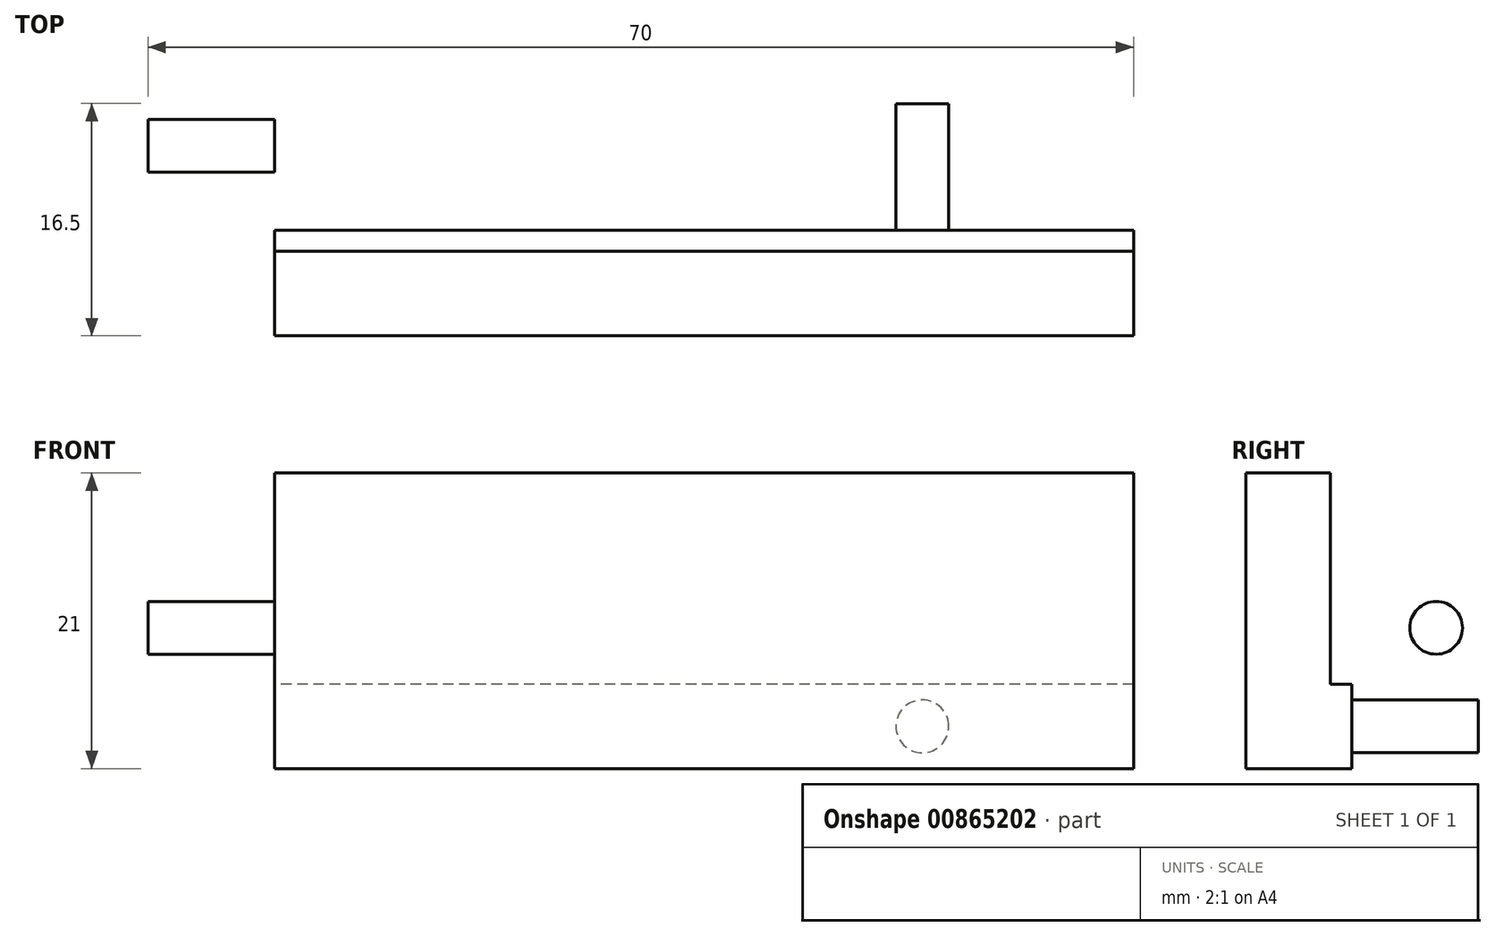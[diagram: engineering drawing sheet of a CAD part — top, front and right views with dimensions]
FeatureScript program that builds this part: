
annotation { "Feature Type Name" : "Feature", "Feature Type Description" : "" }
export const myFeature = defineFeature(function(context is Context, id is Id, definition is map)
    precondition{}
    {
        {
            var Q0;
            Q0=qCreatedBy(makeId("Right.planeOp"),FACE);
            var sketch = newSketch(context, id + "F0", { "sketchPlane" : qUnion([Q0])});
            skLineSegment(sketch, "E0", {"start": v(15.98, 43.88) * mm, "end": v(15.98, -37.12) * mm});
            skLineSegment(sketch, "E1", {"start": v(-0.52, -37.12) * mm, "end": v(15.98, -37.12) * mm});
            skLineSegment(sketch, "E2", {"start": v(-0.52, -37.12) * mm, "end": v(-0.52, -16.12) * mm});
            skLineSegment(sketch, "E3", {"start": v(5.48, -16.12) * mm, "end": v(5.48, -31.12) * mm});
            skLineSegment(sketch, "E4", {"start": v(5.48, -31.12) * mm, "end": v(9.98, -31.12) * mm});
            skLineSegment(sketch, "E5", {"start": v(9.98, -31.12) * mm, "end": v(9.98, 43.88) * mm});
            skLineSegment(sketch, "E6", {"start": v(9.98, 43.88) * mm, "end": v(15.98, 43.88) * mm});
            skLineSegment(sketch, "E7", {"start": v(-0.52, -16.12) * mm, "end": v(5.48, -16.12) * mm});
            skSolve(sketch);
        }
        {
            var Q0;
            Q0=makeQuery(id+"F0.imprint","IMPRINT",FACE,{"disambiguationData":[TD([[makeQuery(id+"F0.imprint","IMPRINT",EDGE,{"derivedFrom":sQuery(id+"F0.wireOp",EDGE,"E0")}),-1.0]])]});
            extrude(context, id + "F1", {"entities" : qUnion([Q0]), "depth" : 70 * mm, "offsetDistance" : 25 * mm});
        }
        {
            var Q0;
            Q0=makeQuery(id+"F1.opExtrude","CAP_FACE",FACE,{"disambiguationData":[OSD([sQuery(id+"F0.wireOp",EDGE,"E0"),sQuery(id+"F0.wireOp",EDGE,"E1"),sQuery(id+"F0.wireOp",EDGE,"E2"),sQuery(id+"F0.wireOp",EDGE,"E3"),sQuery(id+"F0.wireOp",EDGE,"E4"),sQuery(id+"F0.wireOp",EDGE,"E5"),sQuery(id+"F0.wireOp",EDGE,"E6"),sQuery(id+"F0.wireOp",EDGE,"E7")])],"isStart":false});
            var sketch = newSketch(context, id + "F2", { "sketchPlane" : qUnion([Q0])});
            skCircle(sketch, "E8", {"center": v(12.98, 33.88) * mm, "radius": 1.5 * mm});
            skCircle(sketch, "E9", {"center": v(12.96, 13.82) * mm, "radius": 1.5 * mm});
            skCircle(sketch, "E10.MirrorC", {"center": v(12.97, -27.15) * mm, "radius": 1.5 * mm});
            skCircle(sketch, "E11.MirrorC", {"center": v(13, -7.2) * mm, "radius": 1.5 * mm});
            skLineSegment(sketch, "E12", {"start": v(12.98, 33.88) * mm, "end": v(12.98, 43.88) * mm});
            skLineSegment(sketch, "E13", {"start": v(12.98, 13.88) * mm, "end": v(12.98, 33.88) * mm});
            skLineSegment(sketch, "E14", {"start": v(12.98, -7.12) * mm, "end": v(12.98, 13.88) * mm});
            skLineSegment(sketch, "E15", {"start": v(12.98, -27.12) * mm, "end": v(12.98, -7.12) * mm});
            skLineSegment(sketch, "E16", {"start": v(12.98, -27.12) * mm, "end": v(12.98, -37.12) * mm});
            skSolve(sketch);
        }
        {
            var Q0;
            Q0=makeQuery(id+"F2.imprint","IMPRINT",FACE,{"disambiguationData":[TD([[makeQuery(id+"F2.imprint","IMPRINT",EDGE,{"derivedFrom":sQuery(id+"F2.wireOp",EDGE,"E8")}),1.0]])]});
            var Q1;
            Q1=makeQuery(id+"F2.imprint","IMPRINT",FACE,{"disambiguationData":[TD([[makeQuery(id+"F2.imprint","IMPRINT",EDGE,{"derivedFrom":sQuery(id+"F2.wireOp",EDGE,"E9")}),1.0]])]});
            var Q2;
            Q2=makeQuery(id+"F2.imprint","IMPRINT",FACE,{"disambiguationData":[TD([[makeQuery(id+"F2.imprint","IMPRINT",EDGE,{"derivedFrom":sQuery(id+"F2.wireOp",EDGE,"E11.MirrorC")}),-1.0]])]});
            var Q3;
            Q3=makeQuery(id+"F2.imprint","IMPRINT",FACE,{"disambiguationData":[TD([[makeQuery(id+"F2.imprint","IMPRINT",EDGE,{"derivedFrom":sQuery(id+"F2.wireOp",EDGE,"E10.MirrorC")}),-1.0]])]});
            extrude(context, id + "F3", {"entities" : qUnion([Q0, Q1, Q2, Q3]), "operationType" : NewBodyOperationType.ADD, "depth" : 8 * mm, "offsetDistance" : 25 * mm});
        }
        {
            var Q0;
            Q0=makeQuery(id+"F1.opExtrude","CAP_FACE",FACE,{"disambiguationData":[OSD([sQuery(id+"F0.wireOp",EDGE,"E0"),sQuery(id+"F0.wireOp",EDGE,"E1"),sQuery(id+"F0.wireOp",EDGE,"E2"),sQuery(id+"F0.wireOp",EDGE,"E3"),sQuery(id+"F0.wireOp",EDGE,"E4"),sQuery(id+"F0.wireOp",EDGE,"E5"),sQuery(id+"F0.wireOp",EDGE,"E6"),sQuery(id+"F0.wireOp",EDGE,"E7")])],"isStart":true});
            var sketch = newSketch(context, id + "F4", { "sketchPlane" : qUnion([Q0])});
            skCircle(sketch, "E17", {"center": v(-12.98, 33.88) * mm, "radius": 1.88 * mm});
            skCircle(sketch, "E18", {"center": v(-12.98, 13.88) * mm, "radius": 1.88 * mm});
            skCircle(sketch, "E19.MirrorC", {"center": v(-12.98, -27.12) * mm, "radius": 1.88 * mm});
            skLineSegment(sketch, "E20", {"start": v(-12.98, 43.88) * mm, "end": v(-12.98, 33.88) * mm});
            skLineSegment(sketch, "E21", {"start": v(-12.98, 33.88) * mm, "end": v(-12.98, 13.88) * mm});
            skLineSegment(sketch, "E22", {"start": v(-12.98, -27.12) * mm, "end": v(-12.98, -37.12) * mm});
            skLineSegment(sketch, "E23", {"start": v(-12.98, -27.12) * mm, "end": v(-12.98, -7.12) * mm});
            skCircle(sketch, "E24", {"center": v(-12.98, -7.12) * mm, "radius": 1.88 * mm});
            skSolve(sketch);
        }
        {
            var Q0;
            {var subQ0=sQuery(id+"F4.wireOp",EDGE,"E20");var subQ1=sQuery(id+"F4.wireOp",EDGE,"E17");var subQ2=makeQuery(id+"F4.imprint","INTERSECT",VERTEX,{"derivedFrom":[subQ1,subQ0]});Q0=makeQuery(id+"F4.imprint","IMPRINT",FACE,{"disambiguationData":[TD([[makeQuery(id+"F4.imprint","IMPRINT",EDGE,{"disambiguationData":[TD([[subQ2,1.0]])],"derivedFrom":subQ1}),1.0]])]});}
            var Q1;
            {var subQ0=sQuery(id+"F4.wireOp",EDGE,"E20");var subQ1=sQuery(id+"F4.wireOp",EDGE,"E17");var subQ2=makeQuery(id+"F4.imprint","INTERSECT",VERTEX,{"derivedFrom":[subQ1,subQ0]});Q1=makeQuery(id+"F4.imprint","IMPRINT",FACE,{"disambiguationData":[TD([[makeQuery(id+"F4.imprint","IMPRINT",EDGE,{"disambiguationData":[TD([[subQ2,-1.0]])],"derivedFrom":subQ1}),1.0]])]});}
            var Q2;
            Q2=makeQuery(id+"F4.imprint","IMPRINT",FACE,{"disambiguationData":[TD([[makeQuery(id+"F4.imprint","IMPRINT",EDGE,{"derivedFrom":sQuery(id+"F4.wireOp",EDGE,"E18")}),1.0]])]});
            var Q3;
            Q3=makeQuery(id+"F4.imprint","IMPRINT",FACE,{"disambiguationData":[TD([[makeQuery(id+"F4.imprint","IMPRINT",EDGE,{"derivedFrom":sQuery(id+"F4.wireOp",EDGE,"E24")}),1.0]])]});
            var Q4;
            {var subQ0=sQuery(id+"F4.wireOp",EDGE,"E22");var subQ1=sQuery(id+"F4.wireOp",EDGE,"E19.MirrorC");var subQ2=makeQuery(id+"F4.imprint","INTERSECT",VERTEX,{"derivedFrom":[subQ1,subQ0]});Q4=makeQuery(id+"F4.imprint","IMPRINT",FACE,{"disambiguationData":[TD([[makeQuery(id+"F4.imprint","IMPRINT",EDGE,{"disambiguationData":[TD([[subQ2,-1.0]])],"derivedFrom":subQ1}),-1.0]])]});}
            var Q5;
            {var subQ0=sQuery(id+"F4.wireOp",EDGE,"E22");var subQ1=sQuery(id+"F4.wireOp",EDGE,"E19.MirrorC");var subQ2=makeQuery(id+"F4.imprint","INTERSECT",VERTEX,{"derivedFrom":[subQ1,subQ0]});Q5=makeQuery(id+"F4.imprint","IMPRINT",FACE,{"disambiguationData":[TD([[makeQuery(id+"F4.imprint","IMPRINT",EDGE,{"disambiguationData":[TD([[subQ2,1.0]])],"derivedFrom":subQ1}),-1.0]])]});}
            extrude(context, id + "F5", {"entities" : qUnion([Q0, Q1, Q2, Q3, Q4, Q5]), "operationType" : NewBodyOperationType.REMOVE, "oppositeDirection" : true, "depth" : 9 * mm, "offsetDistance" : 25 * mm});
        }
        {
            var Q0;
            Q0=makeQuery(id+"F1.opExtrude","SWEPT_FACE",FACE,{"disambiguationData":[OSD([sQuery(id+"F0.wireOp",EDGE,"E0")])]});
            var sketch = newSketch(context, id + "F6", { "sketchPlane" : qUnion([Q0])});
            skLineSegment(sketch, "E25", {"start": v(0, -37.12) * mm, "end": v(0, -34.12) * mm});
            skCircle(sketch, "E26", {"center": v(-15, -34.12) * mm, "radius": 1.88 * mm});
            skCircle(sketch, "E27", {"center": v(-35, -34.12) * mm, "radius": 1.88 * mm});
            skCircle(sketch, "E28.MirrorC", {"center": v(-55, -34.12) * mm, "radius": 1.88 * mm});
            skSolve(sketch);
        }
        {
            var Q0;
            Q0=makeQuery(id+"F6.imprint","IMPRINT",FACE,{"disambiguationData":[TD([[makeQuery(id+"F6.imprint","IMPRINT",EDGE,{"derivedFrom":sQuery(id+"F6.wireOp",EDGE,"7ed3d595-2089-45ff-891e-2d6305c679fd0.MirrorC")}),-1.0]])]});
            var Q1;
            Q1=makeQuery(id+"F6.imprint","IMPRINT",FACE,{"disambiguationData":[TD([[makeQuery(id+"F6.imprint","IMPRINT",EDGE,{"derivedFrom":sQuery(id+"F6.wireOp",EDGE,"E28.MirrorC")}),-1.0]])]});
            var Q2;
            Q2=makeQuery(id+"F6.imprint","IMPRINT",FACE,{"disambiguationData":[TD([[makeQuery(id+"F6.imprint","IMPRINT",EDGE,{"derivedFrom":sQuery(id+"F6.wireOp",EDGE,"E27")}),1.0]])]});
            var Q3;
            Q3=makeQuery(id+"F6.imprint","IMPRINT",FACE,{"disambiguationData":[TD([[makeQuery(id+"F6.imprint","IMPRINT",EDGE,{"derivedFrom":sQuery(id+"F6.wireOp",EDGE,"E26")}),1.0]])]});
            extrude(context, id + "F7", {"entities" : qUnion([Q0, Q1, Q2, Q3]), "operationType" : NewBodyOperationType.REMOVE, "oppositeDirection" : true, "depth" : 9 * mm, "offsetDistance" : 25 * mm});
        }
    });
